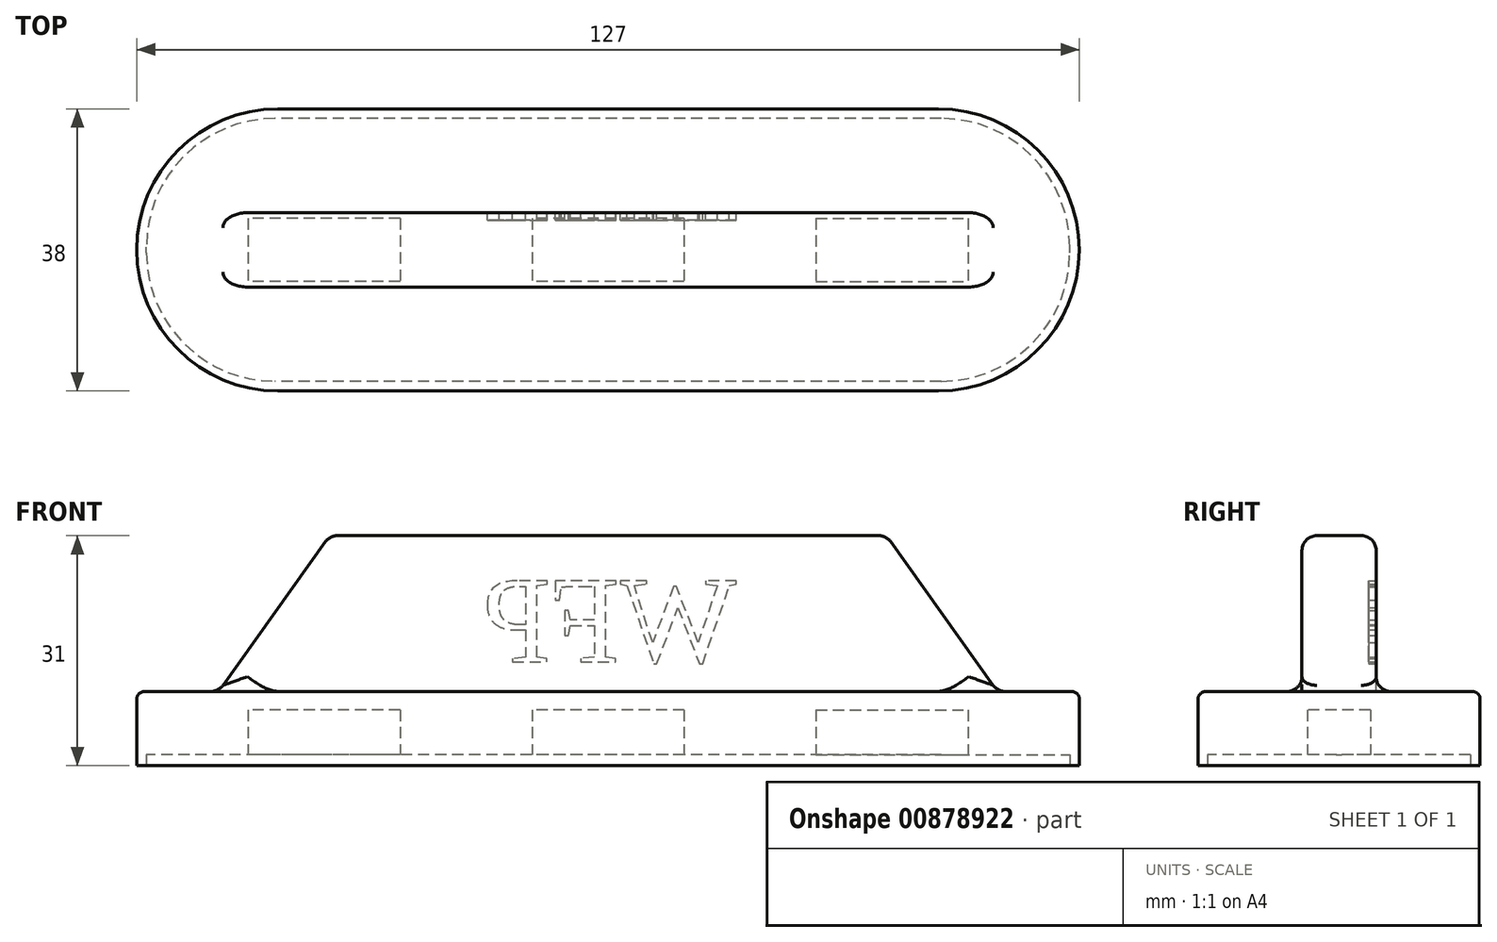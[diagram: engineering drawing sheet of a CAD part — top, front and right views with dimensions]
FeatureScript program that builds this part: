
annotation { "Feature Type Name" : "Feature", "Feature Type Description" : "" }
export const myFeature = defineFeature(function(context is Context, id is Id, definition is map)
    precondition{}
    {
        {
            var Q0;
            Q0=qCreatedBy(makeId("Top.planeOp"),FACE);
            var sketch = newSketch(context, id + "F0", { "sketchPlane" : qUnion([Q0])});
            skLineSegment(sketch, "E0.bottom", {"start": v(44.5, 19) * mm, "end": v(-44.5, 19) * mm});
            skLineSegment(sketch, "E0.top", {"start": v(44.5, -19) * mm, "end": v(-44.5, -19) * mm});
            skLineSegment(sketch, "E0.left", {"start": v(63.5, 0) * mm, "end": v(63.5, 0) * mm});
            skLineSegment(sketch, "E0.right", {"start": v(-63.5, 0) * mm, "end": v(-63.5, 0) * mm});
            skPoint(sketch, "E0.middle", {"position": v(0, 0) * mm});
            skPoint(sketch, "E1.visualSharp", {"position": v(-63.5, 19) * mm});
            skArc(sketch, "E1.filletArc", {"start": v(-44.5, 19) * mm, "mid": v(-57.94, 13.44) * mm, "end": v(-63.5, 0) * mm});
            skPoint(sketch, "E2.visualSharp", {"position": v(-63.5, -19) * mm});
            skArc(sketch, "E2.filletArc", {"start": v(-63.5, 0) * mm, "mid": v(-57.94, -13.44) * mm, "end": v(-44.5, -19) * mm});
            skPoint(sketch, "E3.visualSharp", {"position": v(63.5, 19) * mm});
            skArc(sketch, "E3.filletArc", {"start": v(63.5, 0) * mm, "mid": v(57.94, 13.44) * mm, "end": v(44.5, 19) * mm});
            skPoint(sketch, "E4.visualSharp", {"position": v(63.5, -19) * mm});
            skArc(sketch, "E4.filletArc", {"start": v(44.5, -19) * mm, "mid": v(57.94, -13.44) * mm, "end": v(63.5, 0) * mm});
            skSolve(sketch);
        }
        {
            var Q0;
            Q0 = qSketchRegion(id + "F0", true);
            extrude(context, id + "F1", {"entities" : qUnion([Q0]), "depth" : 10 * mm, "offsetDistance" : 25 * mm});
        }
        {
            var Q0;
            Q0=makeQuery(id+"F1.opExtrude","CAP_FACE",FACE,{"disambiguationData":[OSD([sQuery(id+"F0.wireOp",EDGE,"E0.bottom"),sQuery(id+"F0.wireOp",EDGE,"E0.top"),sQuery(id+"F0.wireOp",EDGE,"E1.filletArc"),sQuery(id+"F0.wireOp",EDGE,"E2.filletArc"),sQuery(id+"F0.wireOp",EDGE,"E3.filletArc"),sQuery(id+"F0.wireOp",EDGE,"E4.filletArc")])],"isStart":false});
            var sketch = newSketch(context, id + "F2", { "sketchPlane" : qUnion([Q0])});
            skLineSegment(sketch, "E5.bottom", {"start": v(52.5, 5) * mm, "end": v(-52.5, 5) * mm});
            skLineSegment(sketch, "E5.top", {"start": v(52.5, -5) * mm, "end": v(-52.5, -5) * mm});
            skLineSegment(sketch, "E5.left", {"start": v(52.5, 5) * mm, "end": v(52.5, -5) * mm});
            skLineSegment(sketch, "E5.right", {"start": v(-52.5, 5) * mm, "end": v(-52.5, -5) * mm});
            skPoint(sketch, "E5.middle", {"position": v(0, 0) * mm});
            skSolve(sketch);
        }
        {
            var Q0;
            Q0 = qSketchRegion(id + "F2", true);
            extrude(context, id + "F3", {"entities" : qUnion([Q0]), "operationType" : NewBodyOperationType.ADD, "depth" : 21 * mm, "offsetDistance" : 25 * mm});
        }
        {
            var Q0;
            Q0=makeQuery(id+"F3.opExtrude","SWEPT_FACE",FACE,{"disambiguationData":[OSD([sQuery(id+"F2.wireOp",EDGE,"E5.top")])]});
            var sketch = newSketch(context, id + "F4", { "sketchPlane" : qUnion([Q0])});
            skLineSegment(sketch, "E6", {"start": v(-52.5, 10) * mm, "end": v(-37.5, 31) * mm});
            skLineSegment(sketch, "E7", {"start": v(-37.5, 31) * mm, "end": v(-52.5, 31) * mm});
            skLineSegment(sketch, "E8", {"start": v(-52.5, 31) * mm, "end": v(-52.5, 10) * mm});
            skLineSegment(sketch, "E9", {"start": v(52.5, 10) * mm, "end": v(37.5, 31) * mm});
            skLineSegment(sketch, "E10", {"start": v(37.5, 31) * mm, "end": v(52.5, 31) * mm});
            skLineSegment(sketch, "E11", {"start": v(52.5, 31) * mm, "end": v(52.5, 10) * mm});
            skSolve(sketch);
        }
        {
            var Q0;
            Q0=makeQuery(id+"F4.imprint","IMPRINT",FACE,{"disambiguationData":[TD([[makeQuery(id+"F4.imprint","IMPRINT",EDGE,{"derivedFrom":sQuery(id+"F4.wireOp",EDGE,"E6")}),1.0]])]});
            var Q1;
            Q1=makeQuery(id+"F4.imprint","IMPRINT",FACE,{"disambiguationData":[TD([[makeQuery(id+"F4.imprint","IMPRINT",EDGE,{"derivedFrom":sQuery(id+"F4.wireOp",EDGE,"E9")}),-1.0]])]});
            extrude(context, id + "F5", {"entities" : qUnion([Q0, Q1]), "operationType" : NewBodyOperationType.REMOVE, "oppositeDirection" : true, "depth" : 10 * mm, "offsetDistance" : 25 * mm});
        }
        {
            var Q0;
            Q0=makeQuery(id+"F5.boolean.opBoolean","COPY",FACE,{"derivedFrom":makeQuery(id+"F5.opExtrude","SWEPT_FACE",FACE,{"disambiguationData":[OSD([sQuery(id+"F4.wireOp",EDGE,"E6")])]})});
            var Q1;
            Q1=makeQuery(id+"F3.opExtrude","CAP_FACE",FACE,{"disambiguationData":[OSD([sQuery(id+"F2.wireOp",EDGE,"E5.bottom"),sQuery(id+"F2.wireOp",EDGE,"E5.top"),sQuery(id+"F2.wireOp",EDGE,"E5.left"),sQuery(id+"F2.wireOp",EDGE,"E5.right")])],"isStart":false});
            var Q2;
            Q2=makeQuery(id+"F5.boolean.opBoolean","COPY",FACE,{"derivedFrom":makeQuery(id+"F5.opExtrude","SWEPT_FACE",FACE,{"disambiguationData":[OSD([sQuery(id+"F4.wireOp",EDGE,"E9")])]})});
            fillet(context, id + "F6", {"entities" : qUnion([Q0, Q1, Q2]), "radius" : 2 * mm, "tangentPropagation" : true, "allowEdgeOverflow" : false});
        }
        {
            var Q0;
            Q0=makeQuery(id+"F1.opExtrude","CAP_FACE",FACE,{"disambiguationData":[OSD([sQuery(id+"F0.wireOp",EDGE,"E0.bottom"),sQuery(id+"F0.wireOp",EDGE,"E0.top"),sQuery(id+"F0.wireOp",EDGE,"E1.filletArc"),sQuery(id+"F0.wireOp",EDGE,"E2.filletArc"),sQuery(id+"F0.wireOp",EDGE,"E3.filletArc"),sQuery(id+"F0.wireOp",EDGE,"E4.filletArc")])],"isStart":true});
            var sketch = newSketch(context, id + "F7", { "sketchPlane" : qUnion([Q0])});
            skPoint(sketch, "E12.middle", {"position": v(0, 0) * mm});
            skLineSegment(sketch, "E13.bottom", {"start": v(44.9, 17.7) * mm, "end": v(-44.9, 17.7) * mm});
            skLineSegment(sketch, "E13.top", {"start": v(44.9, -17.7) * mm, "end": v(-44.9, -17.7) * mm});
            skLineSegment(sketch, "E13.left", {"start": v(62.2, 0.4) * mm, "end": v(62.2, -0.4) * mm});
            skLineSegment(sketch, "E13.right", {"start": v(-62.2, 0.4) * mm, "end": v(-62.2, -0.4) * mm});
            skPoint(sketch, "E14.visualSharp", {"position": v(62.2, 17.7) * mm});
            skArc(sketch, "E14.filletArc", {"start": v(62.2, 0.4) * mm, "mid": v(57.13, 12.63) * mm, "end": v(44.9, 17.7) * mm});
            skPoint(sketch, "E15.visualSharp", {"position": v(62.2, -17.7) * mm});
            skArc(sketch, "E15.filletArc", {"start": v(44.9, -17.7) * mm, "mid": v(57.13, -12.63) * mm, "end": v(62.2, -0.4) * mm});
            skPoint(sketch, "E16.visualSharp", {"position": v(-62.2, -17.7) * mm});
            skArc(sketch, "E16.filletArc", {"start": v(-62.2, -0.4) * mm, "mid": v(-57.13, -12.63) * mm, "end": v(-44.9, -17.7) * mm});
            skPoint(sketch, "E17.visualSharp", {"position": v(-62.2, 17.7) * mm});
            skArc(sketch, "E17.filletArc", {"start": v(-44.9, 17.7) * mm, "mid": v(-57.13, 12.63) * mm, "end": v(-62.2, 0.4) * mm});
            skSolve(sketch);
        }
        {
            var Q0;
            Q0=makeQuery(id+"F7.imprint","IMPRINT",FACE,{"disambiguationData":[TD([[makeQuery(id+"F7.imprint","IMPRINT",EDGE,{"derivedFrom":sQuery(id+"F7.wireOp",EDGE,"E13.bottom")}),1.0]])]});
            extrude(context, id + "F8", {"entities" : qUnion([Q0]), "operationType" : NewBodyOperationType.REMOVE, "oppositeDirection" : true, "depth" : 1.5 * mm, "offsetDistance" : 25 * mm});
        }
        {
            var Q0;
            Q0=makeQuery(id+"F8.boolean.opBoolean","COPY",FACE,{"derivedFrom":makeQuery(id+"F8.opExtrude","CAP_FACE",FACE,{"disambiguationData":[OSD([sQuery(id+"F7.wireOp",EDGE,"E13.bottom"),sQuery(id+"F7.wireOp",EDGE,"E13.top"),sQuery(id+"F7.wireOp",EDGE,"E13.left"),sQuery(id+"F7.wireOp",EDGE,"E13.right"),sQuery(id+"F7.wireOp",EDGE,"E14.filletArc"),sQuery(id+"F7.wireOp",EDGE,"E15.filletArc"),sQuery(id+"F7.wireOp",EDGE,"E16.filletArc"),sQuery(id+"F7.wireOp",EDGE,"E17.filletArc")])],"isStart":false})});
            var sketch = newSketch(context, id + "F9", { "sketchPlane" : qUnion([Q0])});
            skLineSegment(sketch, "E18.bottom", {"start": v(10.25, -4.25) * mm, "end": v(-10.25, -4.25) * mm});
            skLineSegment(sketch, "E18.top", {"start": v(10.25, 4.25) * mm, "end": v(-10.25, 4.25) * mm});
            skLineSegment(sketch, "E18.left", {"start": v(10.25, -4.25) * mm, "end": v(10.25, 4.25) * mm});
            skLineSegment(sketch, "E18.right", {"start": v(-10.25, -4.25) * mm, "end": v(-10.25, 4.25) * mm});
            skPoint(sketch, "E18.middle", {"position": v(0, 0) * mm});
            skLineSegment(sketch, "E19.bottom", {"start": v(28, -4.25) * mm, "end": v(48.5, -4.25) * mm});
            skLineSegment(sketch, "E19.top", {"start": v(28, 4.25) * mm, "end": v(48.5, 4.25) * mm});
            skLineSegment(sketch, "E19.left", {"start": v(28, -4.25) * mm, "end": v(28, 4.25) * mm});
            skLineSegment(sketch, "E19.right", {"start": v(48.5, -4.25) * mm, "end": v(48.5, 4.25) * mm});
            skPoint(sketch, "E19.middle", {"position": v(38.25, 0) * mm});
            skLineSegment(sketch, "E20.bottom", {"start": v(-28, -4.25) * mm, "end": v(-48.5, -4.25) * mm});
            skLineSegment(sketch, "E20.top", {"start": v(-28, 4.25) * mm, "end": v(-48.5, 4.25) * mm});
            skLineSegment(sketch, "E20.left", {"start": v(-28, -4.25) * mm, "end": v(-28, 4.25) * mm});
            skLineSegment(sketch, "E20.right", {"start": v(-48.5, -4.25) * mm, "end": v(-48.5, 4.25) * mm});
            skPoint(sketch, "E20.middle", {"position": v(-38.25, 0) * mm});
            skSolve(sketch);
        }
        {
            var Q0;
            Q0=makeQuery(id+"F9.imprint","IMPRINT",FACE,{"disambiguationData":[TD([[makeQuery(id+"F9.imprint","IMPRINT",EDGE,{"derivedFrom":sQuery(id+"F9.wireOp",EDGE,"E19.bottom")}),1.0]])]});
            var Q1;
            Q1=makeQuery(id+"F9.imprint","IMPRINT",FACE,{"disambiguationData":[TD([[makeQuery(id+"F9.imprint","IMPRINT",EDGE,{"derivedFrom":sQuery(id+"F9.wireOp",EDGE,"E18.bottom")}),-1.0]])]});
            var Q2;
            Q2=makeQuery(id+"F9.imprint","IMPRINT",FACE,{"disambiguationData":[TD([[makeQuery(id+"F9.imprint","IMPRINT",EDGE,{"derivedFrom":sQuery(id+"F9.wireOp",EDGE,"E20.bottom")}),-1.0]])]});
            extrude(context, id + "F10", {"entities" : qUnion([Q0, Q1, Q2]), "operationType" : NewBodyOperationType.REMOVE, "oppositeDirection" : true, "depth" : 6 * mm, "offsetDistance" : 25 * mm});
        }
        {
            var Q0;
            Q0=makeQuery(id+"F1.opExtrude","CAP_EDGE",EDGE,{"disambiguationData":[OSD([sQuery(id+"F0.wireOp",EDGE,"E0.bottom")])],"isStart":false});
            fillet(context, id + "F11", {"entities" : qUnion([Q0]), "radius" : 1 * mm, "tangentPropagation" : true, "allowEdgeOverflow" : false});
        }
        {
            var Q0;
            Q0=makeQuery(id+"F3.opExtrude","SWEPT_FACE",FACE,{"disambiguationData":[OSD([sQuery(id+"F2.wireOp",EDGE,"E5.bottom")])]});
            var sketch = newSketch(context, id + "F12", { "sketchPlane" : qUnion([Q0])});
            skText(sketch, "E21", { "text": "WFP", "fontName": "Tinos-Regular.ttf"});
            const initialGuessF12  = {"E21": [-0.01732, 0.014, 1, 0, 0.012]};
            skSetInitialGuess(sketch, initialGuessF12);
            skSolve(sketch);
        }
        {
            var Q0;
            Q0 = qSketchRegion(id + "F12", true);
            extrude(context, id + "F13", {"entities" : qUnion([Q0]), "operationType" : NewBodyOperationType.REMOVE, "oppositeDirection" : true, "depth" : 1 * mm, "offsetDistance" : 25 * mm});
        }
    });
